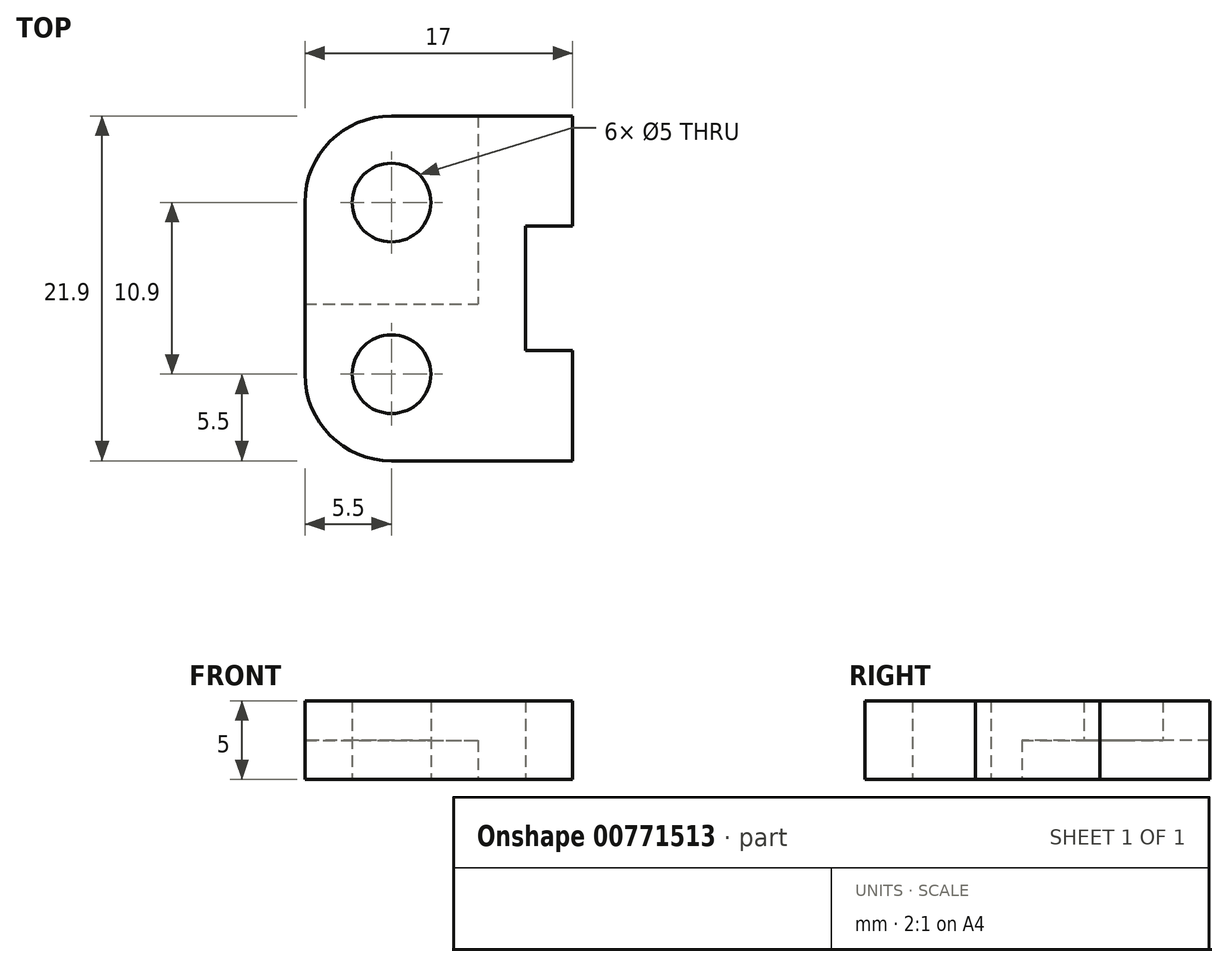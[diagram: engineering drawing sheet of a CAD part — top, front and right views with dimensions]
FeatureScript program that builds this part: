
annotation { "Feature Type Name" : "Feature", "Feature Type Description" : "" }
export const myFeature = defineFeature(function(context is Context, id is Id, definition is map)
    precondition{}
    {
        {
            var Q0;
            Q0=qCreatedBy(makeId("Top.planeOp"),FACE);
            var sketch = newSketch(context, id + "F0", { "sketchPlane" : qUnion([Q0])});
            skCircle(sketch, "E0", {"center": v(0, 0) * mm, "radius": 2.5 * mm});
            skLineSegment(sketch, "E1", {"start": v(0, 0) * mm, "end": v(-2.5, 0) * mm, "construction": true});
            skLineSegment(sketch, "E2", {"start": v(-2.5, 0) * mm, "end": v(2.5, 0) * mm, "construction": true});
            skArc(sketch, "E3", {"start": v(-5.5, 0) * mm, "mid": v(0, -5.5) * mm, "end": v(5.5, 0) * mm});
            skLineSegment(sketch, "E4", {"start": v(-5.5, 0) * mm, "end": v(-5.5, 10.9) * mm});
            skLineSegment(sketch, "E5", {"start": v(-2.5, 10.9) * mm, "end": v(2.5, 10.9) * mm});
            skLineSegment(sketch, "E6", {"start": v(5.5, 10.9) * mm, "end": v(5.5, 0) * mm});
            skCircle(sketch, "E7", {"center": v(0, 10.9) * mm, "radius": 2.5 * mm});
            skArc(sketch, "E8", {"start": v(-5.5, 10.9) * mm, "mid": v(0, 16.4) * mm, "end": v(5.5, 10.9) * mm});
            skLineSegment(sketch, "E9", {"start": v(-5.5, 5.45) * mm, "end": v(-5.5, 4.45) * mm});
            skLineSegment(sketch, "E10", {"start": v(-5.5, 4.45) * mm, "end": v(5.5, 4.45) * mm});
            skLineSegment(sketch, "E11", {"start": v(0, 16.4) * mm, "end": v(11.5, 16.4) * mm});
            skLineSegment(sketch, "E12", {"start": v(11.5, 16.4) * mm, "end": v(11.5, -5.5) * mm});
            skLineSegment(sketch, "E13", {"start": v(11.5, -5.5) * mm, "end": v(0, -5.5) * mm});
            skLineSegment(sketch, "E14", {"start": v(5.5, 10.9) * mm, "end": v(5.5, 16.4) * mm});
            skLineSegment(sketch, "E15.bottom", {"start": v(11.5, -5.5) * mm, "end": v(8.5, -5.5) * mm});
            skLineSegment(sketch, "E15.top", {"start": v(11.5, 1.5) * mm, "end": v(8.5, 1.5) * mm});
            skLineSegment(sketch, "E15.left", {"start": v(11.5, -5.5) * mm, "end": v(11.5, 1.5) * mm});
            skLineSegment(sketch, "E15.right", {"start": v(8.5, -5.5) * mm, "end": v(8.5, 1.5) * mm});
            skLineSegment(sketch, "E16.bottom", {"start": v(11.5, 16.4) * mm, "end": v(8.5, 16.4) * mm});
            skLineSegment(sketch, "E16.top", {"start": v(11.5, 9.4) * mm, "end": v(8.5, 9.4) * mm});
            skLineSegment(sketch, "E16.left", {"start": v(11.5, 16.4) * mm, "end": v(11.5, 9.4) * mm});
            skLineSegment(sketch, "E16.right", {"start": v(8.5, 16.4) * mm, "end": v(8.5, 9.4) * mm});
            skLineSegment(sketch, "E17", {"start": v(8.5, 9.4) * mm, "end": v(8.5, 1.5) * mm});
            skSolve(sketch);
        }
        {
            var Q0;
            Q0=makeQuery(id+"F0.imprint","IMPRINT",FACE,{"disambiguationData":[TD([[makeQuery(id+"F0.imprint","IMPRINT",EDGE,{"derivedFrom":sQuery(id+"F0.wireOp",EDGE,"E0")}),-1.0]])]});
            var Q1;
            {var subQ7=sQuery(id+"F0.wireOp",EDGE,"E10");Q1=makeQuery(id+"F0.imprint","IMPRINT",FACE,{"disambiguationData":[TD([[makeQuery(id+"F0.imprint","IMPRINT",EDGE,{"derivedFrom":subQ7}),1.0]])]});}
            var Q2;
            {var subQ0=sQuery(id+"F0.wireOp",EDGE,"E14");Q2=makeQuery(id+"F0.imprint","IMPRINT",FACE,{"disambiguationData":[TD([[makeQuery(id+"F0.imprint","IMPRINT",EDGE,{"derivedFrom":subQ0}),1.0]])]});}
            var Q3;
            {var subQ2=sQuery(id+"F0.wireOp",EDGE,"E14");Q3=makeQuery(id+"F0.imprint","IMPRINT",FACE,{"disambiguationData":[TD([[makeQuery(id+"F0.imprint","IMPRINT",EDGE,{"derivedFrom":subQ2}),-1.0]])]});}
            var Q4;
            {var subQ0=sQuery(id+"F0.wireOp",EDGE,"E14");Q4=makeQuery(id+"F0.imprint","IMPRINT",FACE,{"disambiguationData":[TD([[makeQuery(id+"F0.imprint","IMPRINT",EDGE,{"derivedFrom":subQ0}),1.0]])]});}
            var Q5;
            {var subQ0=sQuery(id+"F0.wireOp",EDGE,"E15.top");Q5=makeQuery(id+"F0.imprint","IMPRINT",FACE,{"disambiguationData":[TD([[makeQuery(id+"F0.imprint","IMPRINT",EDGE,{"derivedFrom":subQ0}),1.0]])]});}
            var Q6;
            {var subQ4=sQuery(id+"F0.wireOp",EDGE,"E16.top");Q6=makeQuery(id+"F0.imprint","IMPRINT",FACE,{"disambiguationData":[TD([[makeQuery(id+"F0.imprint","IMPRINT",EDGE,{"derivedFrom":subQ4}),-1.0]])]});}
            extrude(context, id + "F1", {"entities" : qUnion([Q0, Q1, Q2, Q3, Q4, Q5, Q6]), "depth" : 5 * mm, "offsetDistance" : 25 * mm});
        }
        {
            var Q0;
            {var subQ7=sQuery(id+"F0.wireOp",EDGE,"E10");Q0=makeQuery(id+"F0.imprint","IMPRINT",FACE,{"disambiguationData":[TD([[makeQuery(id+"F0.imprint","IMPRINT",EDGE,{"derivedFrom":subQ7}),1.0]])]});}
            var Q1;
            {var subQ0=sQuery(id+"F0.wireOp",EDGE,"E14");Q1=makeQuery(id+"F0.imprint","IMPRINT",FACE,{"disambiguationData":[TD([[makeQuery(id+"F0.imprint","IMPRINT",EDGE,{"derivedFrom":subQ0}),1.0]])]});}
            var Q2;
            {var subQ0=sQuery(id+"F0.wireOp",EDGE,"E14");Q2=makeQuery(id+"F0.imprint","IMPRINT",FACE,{"disambiguationData":[TD([[makeQuery(id+"F0.imprint","IMPRINT",EDGE,{"derivedFrom":subQ0}),1.0]])]});}
            extrude(context, id + "F2", {"entities" : qUnion([Q0, Q1, Q2]), "operationType" : NewBodyOperationType.REMOVE, "depth" : 2.5 * mm, "offsetDistance" : 25 * mm});
        }
    });
